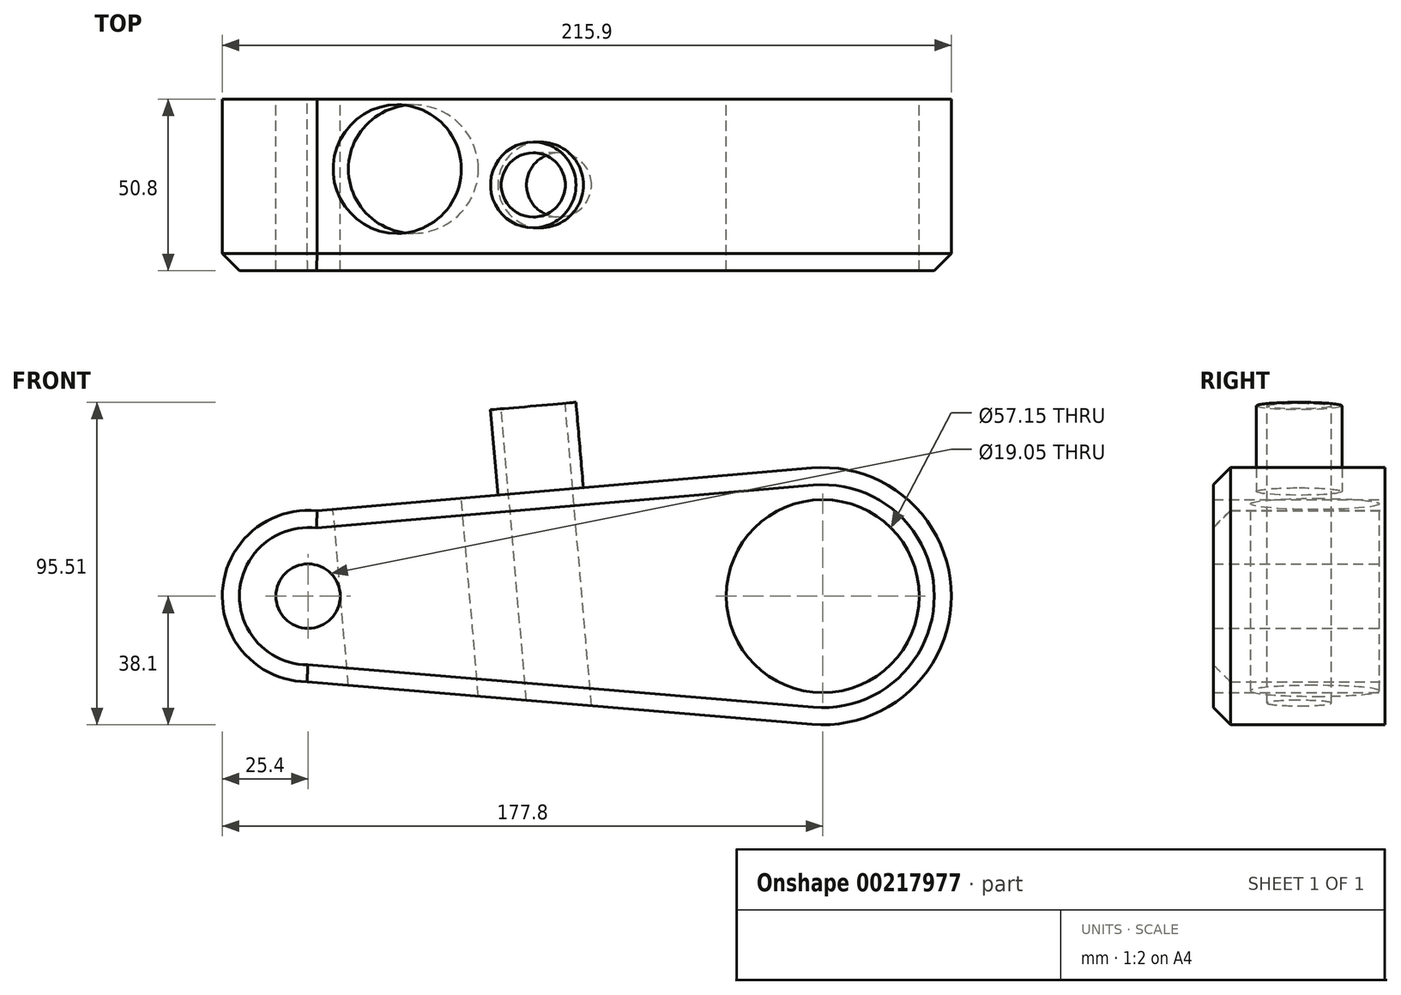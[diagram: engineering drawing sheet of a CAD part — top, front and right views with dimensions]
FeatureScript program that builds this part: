
annotation { "Feature Type Name" : "Feature", "Feature Type Description" : "" }
export const myFeature = defineFeature(function(context is Context, id is Id, definition is map)
    precondition{}
    {
        {
            var Q0;
            Q0=qCreatedBy(makeId("Front.planeOp"),FACE);
            var sketch = newSketch(context, id + "F0", { "sketchPlane" : qUnion([Q0])});
            skCircle(sketch, "E0", {"center": v(0, 0) * mm, "radius": 38.1 * mm});
            skCircle(sketch, "E1", {"center": v(-152.4, 0) * mm, "radius": 25.4 * mm});
            skLineSegment(sketch, "E2", {"start": v(-149.78, 25.26) * mm, "end": v(0, 38.24) * mm});
            skLineSegment(sketch, "E3", {"start": v(-152.7, -25.4) * mm, "end": v(-3.2, -37.97) * mm});
            skSolve(sketch);
        }
        {
            var Q0;
            Q0 = qSketchRegion(id + "F0", true);
            extrude(context, id + "F1", {"entities" : qUnion([Q0]), "depth" : 50.8 * mm});
        }
        {
            var Q0;
            Q0=makeQuery(id+"F1.opExtrude","SWEPT_FACE",FACE,{"disambiguationData":[OSD([sQuery(id+"F0.wireOp",EDGE,"E2")])]});
            var sketch = newSketch(context, id + "F2", { "sketchPlane" : qUnion([Q0])});
            skCircle(sketch, "E4", {"center": v(-80.55, -25.4) * mm, "radius": 12.7 * mm});
            skPoint(sketch, "E4.centerSnap0", {"position": v(0, -25.4) * mm});
            skSolve(sketch);
        }
        {
            var Q0;
            Q0 = qSketchRegion(id + "F2", true);
            extrude(context, id + "F3", {"entities" : qUnion([Q0]), "operationType" : NewBodyOperationType.ADD, "depth" : 25.4 * mm});
        }
        {
            var Q0;
            Q0=makeQuery(id+"F1.opExtrude","CAP_FACE",FACE,{"disambiguationData":[OSD([sQuery(id+"F0.wireOp",EDGE,"E0"),sQuery(id+"F0.wireOp",EDGE,"E1"),sQuery(id+"F0.wireOp",EDGE,"E2"),sQuery(id+"F0.wireOp",EDGE,"E3")])],"isStart":false});
            chamfer(context, id + "F4", {"entities" : qUnion([Q0]), "width" : 5.08 * mm, "tangentPropagation" : true});
        }
        {
            var Q0;
            Q0=makeQuery(id+"F1.opExtrude","CAP_FACE",FACE,{"disambiguationData":[OSD([sQuery(id+"F0.wireOp",EDGE,"E0"),sQuery(id+"F0.wireOp",EDGE,"E1"),sQuery(id+"F0.wireOp",EDGE,"E2"),sQuery(id+"F0.wireOp",EDGE,"E3")])],"isStart":true});
            var sketch = newSketch(context, id + "F5", { "sketchPlane" : qUnion([Q0])});
            skCircle(sketch, "E5", {"center": v(0, 0) * mm, "radius": 27.06 * mm});
            skCircle(sketch, "E6", {"center": v(152.4, 0) * mm, "radius": 15.78 * mm});
            skSolve(sketch);
        }
        {
            var Q0;
            Q0=sQuery(id+"F5.wireOp",VERTEX,"E5.center");
            var Q1;
            Q1=makeQuery(id+"F1.opExtrude","SWEPT_BODY",BODY,{"disambiguationData":[OSD([sQuery(id+"F0.wireOp",EDGE,"E0"),sQuery(id+"F0.wireOp",EDGE,"E1"),sQuery(id+"F0.wireOp",EDGE,"E2"),sQuery(id+"F0.wireOp",EDGE,"E3")])]});
            hole(context, id + "F6", {"style" : HoleStyle.SIMPLE, "endStyle" : HoleEndStyle.THROUGH, "holeDiameter" : 57.15 * mm, "locations" : qUnion([Q0]), "scope" : qUnion([Q1]), "isTappedThrough" : true});
        }
        {
            var Q0;
            Q0=makeQuery(id+"F1.opExtrude","CAP_FACE",FACE,{"disambiguationData":[OSD([sQuery(id+"F0.wireOp",EDGE,"E0"),sQuery(id+"F0.wireOp",EDGE,"E1"),sQuery(id+"F0.wireOp",EDGE,"E2"),sQuery(id+"F0.wireOp",EDGE,"E3")])],"isStart":false});
            extrude(context, id + "F7", {"entities" : qUnion([Q0]), "operationType" : NewBodyOperationType.ADD, "oppositeDirection" : true, "depth" : 6.1 * mm});
        }
        {
            var Q0;
            Q0=makeQuery(id+"F3.opExtrude","CAP_FACE",FACE,{"disambiguationData":[OSD([sQuery(id+"F2.wireOp",EDGE,"E4")])],"isStart":false});
            var sketch = newSketch(context, id + "F8", { "sketchPlane" : qUnion([Q0])});
            skCircle(sketch, "E7", {"center": v(-80.55, -25.4) * mm, "radius": 9.1 * mm});
            skSolve(sketch);
        }
        {
            var Q0;
            Q0=sQuery(id+"F8.wireOp",VERTEX,"E7.center");
            var Q1;
            Q1=makeQuery(id+"F1.opExtrude","SWEPT_BODY",BODY,{"disambiguationData":[OSD([sQuery(id+"F0.wireOp",EDGE,"E0"),sQuery(id+"F0.wireOp",EDGE,"E1"),sQuery(id+"F0.wireOp",EDGE,"E2"),sQuery(id+"F0.wireOp",EDGE,"E3")])]});
            hole(context, id + "F9", {"style" : HoleStyle.SIMPLE, "endStyle" : HoleEndStyle.THROUGH, "holeDiameter" : 19.05 * mm, "locations" : qUnion([Q0]), "scope" : qUnion([Q1]), "isTappedThrough" : true});
        }
        {
            var Q0;
            Q0=makeQuery(id+"F1.opExtrude","CAP_FACE",FACE,{"disambiguationData":[OSD([sQuery(id+"F0.wireOp",EDGE,"E0"),sQuery(id+"F0.wireOp",EDGE,"E1"),sQuery(id+"F0.wireOp",EDGE,"E2"),sQuery(id+"F0.wireOp",EDGE,"E3")])],"isStart":true});
            var sketch = newSketch(context, id + "F10", { "sketchPlane" : qUnion([Q0])});
            skCircle(sketch, "E8", {"center": v(152.4, 0) * mm, "radius": 8.87 * mm});
            skSolve(sketch);
        }
        {
            var Q0;
            Q0=sQuery(id+"F10.wireOp",VERTEX,"E8.center");
            var Q1;
            Q1=makeQuery(id+"F1.opExtrude","SWEPT_BODY",BODY,{"disambiguationData":[OSD([sQuery(id+"F0.wireOp",EDGE,"E0"),sQuery(id+"F0.wireOp",EDGE,"E1"),sQuery(id+"F0.wireOp",EDGE,"E2"),sQuery(id+"F0.wireOp",EDGE,"E3")])]});
            hole(context, id + "F11", {"style" : HoleStyle.SIMPLE, "endStyle" : HoleEndStyle.THROUGH, "holeDiameter" : 19.05 * mm, "locations" : qUnion([Q0]), "scope" : qUnion([Q1]), "isTappedThrough" : true});
        }
        {
            var Q0;
            Q0=makeQuery(id+"F1.opExtrude","SWEPT_FACE",FACE,{"disambiguationData":[OSD([sQuery(id+"F0.wireOp",EDGE,"E2")])]});
            var sketch = newSketch(context, id + "F12", { "sketchPlane" : qUnion([Q0])});
            skCircle(sketch, "E9", {"center": v(-123.2, -20.7) * mm, "radius": 5.02 * mm});
            skSolve(sketch);
        }
        {
            var Q0;
            Q0=sQuery(id+"F12.wireOp",VERTEX,"E9.center");
            var Q1;
            Q1=makeQuery(id+"F1.opExtrude","SWEPT_BODY",BODY,{"disambiguationData":[OSD([sQuery(id+"F0.wireOp",EDGE,"E0"),sQuery(id+"F0.wireOp",EDGE,"E1"),sQuery(id+"F0.wireOp",EDGE,"E2"),sQuery(id+"F0.wireOp",EDGE,"E3")])]});
            hole(context, id + "F13", {"style" : HoleStyle.SIMPLE, "endStyle" : HoleEndStyle.THROUGH, "holeDiameter" : 38.1 * mm, "locations" : qUnion([Q0]), "scope" : qUnion([Q1]), "isTappedThrough" : true});
        }
    });
